# Revit family: NBS_DudleyIndustriesLimited_PprTwlDpnsrs_ModuloPaperTowelDispenser
name_source: partatom
category: Generic Models
revit_build: Autodesk Revit 2017 (Build: 20171027_0315(x64)
units: mm (PartAtom-declared; Revit-internal decimal feet)

## family parameters
Always vertical = Yes
Can host rebar = No
Cut with Voids When Loaded = No
Part Type = Normal
Room Calculation Point = No
Round Connector Dimension = Use Diameter
Shared = No
Work Plane-Based = No

## types (1)
- ModuloPaperTowelDispenser
    AssetType = Fixed
    BIMObjectName = NBS_DudleyIndustriesLimited_PaperTowelDispensers_ModuloPaperTowelDispenser
    BlankPlate = NBS_Concept
    Category = Pr_40_70_22_62:Paper towel dispensers
    Color = Black
    Depth = 193 mm
    Description = Autocut Paper Towel Dispenser provides a hygienic hand drying solution
    DurationUnit = year
    ExpectedLife = 10
    Features = Fits the modulo behind the mirror system, provides a hygienic solution as user only touches the paper towel dispensed  no need to touch the unit helping to reduce cleaning requirements, consumables not accessible and kept free from contamination by lockable cabinet cover, quick and easy to refill, suitable for most multi-fold paper towels, spare consumables can be conveniently stored on the shelf within the cabinet, utilises a full modular cabinet space, blanking plates available separately if required
    Finish = Matte black powder coated
    Form = Fits the modulo behind the mirror system
    Grade = Zinc coated mild steel
    HasBlankPlate = No
    IfcExportAs = IfcFurnitureType
    IfcExportType = NOTDEFINED
    IsBuiltIn = Yes
    Length = 383 mm
    ManufacturerName = Dudley Industries Limited
    ManufacturerURL = https://www.dudleyindustries.com
    Material = Stainless steel
    MaterialsBody = Zinc coated mild steel
    MaterialsFinishAndColour = Black
    ModelNumber = 92378BK
    ModelReference = Modulo Paper Towel Dispenser
    NBSCertification = www.nationalbimlibrary.com/cert/j30njvog
    NBSDescription = Paper towel dispensers
    NBSReference = 45-35-72/344
    Name = PaperTowelDispensers_ModuloPaperTowelDispenser_DudleyIndustriesLimited
    NominalDepth = 193 mm
    NominalHeight = 320 mm
    NominalLength = 388 mm
    NominalWidth = 0 mm  [stored 0 ft]
    Operation = Manual
    PaperSleeveMaterial = NBS_Concept
    Size = 388 x 320 x 193 mm
    Status = New
    Style = Paper towel dispenser
    TowelsTowelType = Z Fold
    TowelsWidth = 250mm Max
    Uniclass2015Code = Pr_40_70_22_62
    Uniclass2015Title = Paper towel dispensers
    Uniclass2015Version = Products v1.12
    Version = 1
    WarrantyDescription = 10 years
    WarrantyDurationUnit = year

note: [stored X ft] marks values corroborated as IEEE doubles in the binary element streams (Revit-internal decimal feet)

## geometry (parser evidence)
native form markers: Sweep x2
no freeform markers — native parametric forms only
